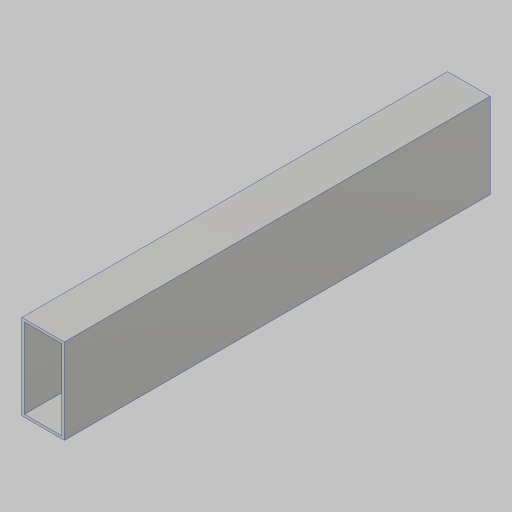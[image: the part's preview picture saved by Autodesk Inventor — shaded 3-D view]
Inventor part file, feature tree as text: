
AUTODESK INVENTOR PART (.ipt)
format: ipt  version: 2023.5 (Build 275446000, 446)  size: 95,744 bytes
history: native  units: in
note: dims shown in document units (in); Inventor stores cm internally (conversion verified against a paired STEP export)
features: extrude x1
ambient origin geometry x8: Origin, YZ Plane, XZ Plane, XY Plane, X Axis, Y Axis, Z Axis, Center Point
bodies: Solid1 (feature_tree)
feature tree (1):
  extrude  "Extrusion1"  TaperAngle=0.0deg  [1 undecoded]
note: 1 required parameter value undecoded (feature->parameter linkage not recoverable at this tier; creation-order binding heuristic only, values carry confidence <= 0.55)
